# Revit family: Toilet-Floor_Mount-KOHLER-Wellworth-K-3987
name_source: partatom
category: Plumbing Fixtures
revit_build: Autodesk Revit 2015 (Build: 20140606_1530(x64)
units: mm (PartAtom-declared; Revit-internal decimal feet)

## types (7) — shared parameters
ADA Compliant = No
Assembly Code = D2010100
CW Connection = Yes
Cold Water Inlet = Cold Water Inlet
Date Modified = 06/21/2019
Default Elevation = 0"
Flow Rate = 0 GPM
Flush Rate- GPF = 1.6 GPF
Flush Rate- LPF = 6.0 LPF
HW Connection = No
Height = 29 1/4"
Hot Water Inlet = Hot Water Inlet
Length = 27 3/4"
Manufacturer = KOHLER Co.
MasterFormat 1995 = 15410
MasterFormat 2004 = 22.41.13
Material = Vitreous China
Pressure = 0.00 psi
Product Documentation Link = https://www.us.kohler.com
Product Name = Wellworth
Product Page URL = http://www.us.kohler.com
Rough-In = 12"
Seat Included = No
URL = https://www.us.kohler.com
Vent Connection = No
Waste Connection = Yes
Waste Water Outlet = Waste Water Outlet
WaterSense Certified = Yes
Width = 18"

## per-type parameters (varying)
| type | 3987_L | 3987_R | Description | Finish | Model | Type |
| Left Hand Trip Lever, 0-White | Yes | No | two-piece round-front dual-flush toilet with Class Five flush technology and left-hand trip lever, seat not included | Kohler-Vitreous_China-0-White | K-3987-0 | 1 |
| Left Hand Trip Lever, 96-Biscuit | Yes | No | two-piece round-front dual-flush toilet with Class Five flush technology and left-hand trip lever, seat not included | Kohler-Vitreous_China-96-Biscuit | K-3987-96 | 2 |
| Left Hand Trip Lever, 47-Almond | Yes | No | two-piece round-front dual-flush toilet with Class Five flush technology and left-hand trip lever, seat not included | Kohler-Vitreous_China-47-Almond | K-3987-47 | 3 |
| Left Hand Trip Lever, 7-Black Black | Yes | No | two-piece round-front dual-flush toilet with Class Five flush technology and left-hand trip lever, seat not included | Kohler-Vitreous_China-7-Black_Black | K-3987-7 | 4 |
| Right Hand Trip Lever, 0-White | No | Yes | two-piece round-front dual-flush toilet with Class Five flush technology and right-hand trip lever, seat not included | Kohler-Vitreous_China-0-White | K-3987-RA-0 | 5 |
| Right Hand Trip Lever, 96-Biscuit | No | Yes | two-piece round-front dual-flush toilet with Class Five flush technology and right-hand trip lever, seat not included | Kohler-Vitreous_China-96-Biscuit | K-3987-RA-96 | 6 |
| Right Hand Trip Lever, 47-Almond | No | Yes | two-piece round-front dual-flush toilet with Class Five flush technology and right-hand trip lever, seat not included | Kohler-Vitreous_China-47-Almond | K-3987-RA-47 | 7 |

## geometry (parser evidence)
native form markers: Sweep x5
no freeform markers — native parametric forms only
